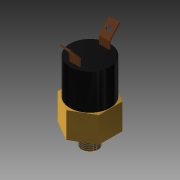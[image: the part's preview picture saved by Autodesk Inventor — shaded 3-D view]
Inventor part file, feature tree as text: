
AUTODESK INVENTOR PART (.ipt)
format: ipt  version: 2018 (Build 220112000, 112)  size: 180,736 bytes
history: native  units: mm (DEFAULTED — no unit token found)
features: extrude x6, sketch x6, projected_geometry x4, mirror x1, thread x1, chamfer x1, fillet x1
ambient origin geometry x8: Origin, YZ Plane, XZ Plane, XY Plane, X Axis, Y Axis, Z Axis, Center Point
bodies: Solid1 (feature_tree)
feature tree (20):
  extrude  "Extrusion1"  Depth=15.875mm TaperAngle=0.0deg
  extrude  "Extrusion2"  Depth=11.049mm TaperAngle=0.0deg
  extrude  "Extrusion3"  Depth=19.9898mm TaperAngle=0.0deg
  extrude  "Extrusion4"  Depth=21.971mm TaperAngle=0.0deg
  extrude  "Extrusion5"  Depth=0.762mm
  extrude  "Extrusion6"  Depth=3.175mm
  mirror  "Mirror1"
  thread  "Thread1"  [1 undecoded]
  chamfer  "Chamfer1"  Distance=6.35mm
  fillet  "Fillet1"  Radius=6.35mm
  sketch  "Sketch1"  dims[d0=25.4mm d1=15.875mm d2=0.0mm]
  sketch  "Sketch2"  dims[d3=10.16mm d4=11.049mm d5=0.0mm]
  projected_geometry  "Projected Loop1"
  sketch  "Sketch3"  dims[d6=3.175mm d7=19.9898mm d8=0.0mm]
  sketch  "Sketch4"  dims[d9=24.765mm d10=21.971mm d11=0.0mm]
  projected_geometry  "Projected Loop2"
  sketch  "Sketch5"  dims[d12=19.05mm d13=0.762mm]
  projected_geometry  "Projected Loop3"
  sketch  "Sketch6"  dims[d14=0.762mm d15=4.699mm d17=9.398mm d18=6.35mm d19=0.0mm d20=6.35mm d21=0.0mm d22=25.4mm d23=0.0mm d24=1.0mm d25=3.175mm d26=45.0deg d27=3.175mm]
  projected_geometry  "Projected Loop4"
note: 1 required parameter value undecoded (feature->parameter linkage not recoverable at this tier; creation-order binding heuristic only, values carry confidence <= 0.55)
